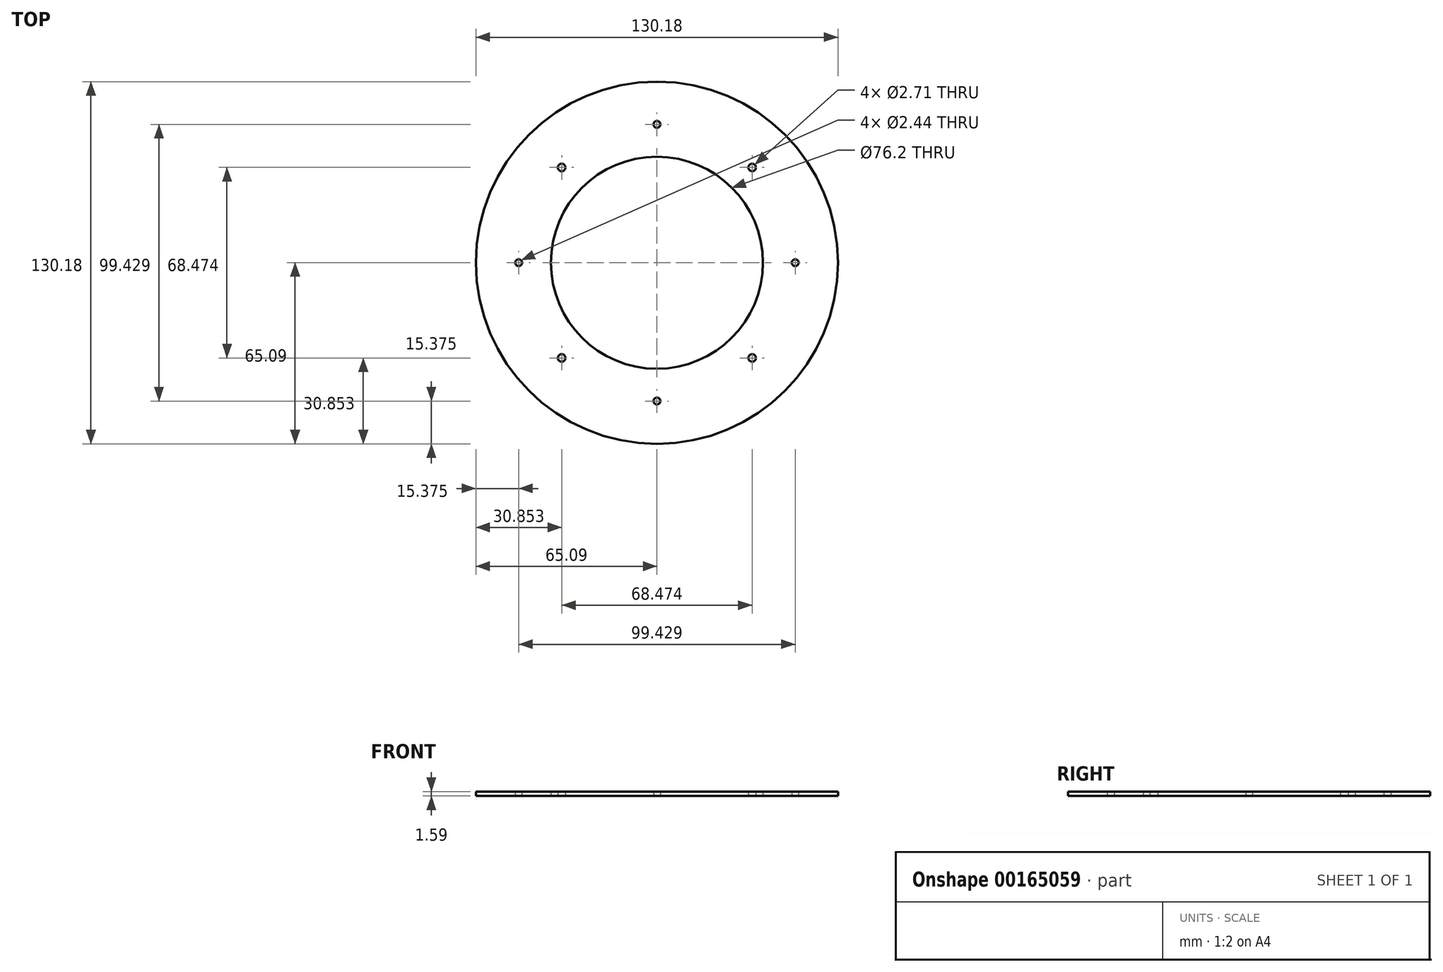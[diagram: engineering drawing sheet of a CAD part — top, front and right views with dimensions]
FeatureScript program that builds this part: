
annotation { "Feature Type Name" : "Feature", "Feature Type Description" : "" }
export const myFeature = defineFeature(function(context is Context, id is Id, definition is map)
    precondition{}
    {
        {
            var Q0;
            Q0=qCreatedBy(makeId("Top.planeOp"),FACE);
            var sketch = newSketch(context, id + "F0", { "sketchPlane" : qUnion([Q0])});
            skLineSegment(sketch, "E0.bottom", {"start": v(49.71, 0) * mm, "end": v(0, 49.71) * mm, "construction": true});
            skLineSegment(sketch, "E0.top", {"start": v(0, -49.71) * mm, "end": v(-49.71, 0) * mm, "construction": true});
            skLineSegment(sketch, "E0.left", {"start": v(49.71, 0) * mm, "end": v(0, -49.71) * mm, "construction": true});
            skLineSegment(sketch, "E0.right", {"start": v(0, 49.71) * mm, "end": v(-49.71, 0) * mm, "construction": true});
            skPoint(sketch, "E0.middle", {"position": v(0, 0) * mm});
            skCircle(sketch, "E1", {"center": v(0, 0) * mm, "radius": 38.1 * mm});
            skCircle(sketch, "E2", {"center": v(49.71, 0) * mm, "radius": 1.22 * mm});
            skCircle(sketch, "E3", {"center": v(0, 49.71) * mm, "radius": 1.22 * mm});
            skCircle(sketch, "E4", {"center": v(-49.71, 0) * mm, "radius": 1.22 * mm});
            skCircle(sketch, "E5", {"center": v(0, -49.71) * mm, "radius": 1.22 * mm});
            skCircle(sketch, "E6", {"center": v(0, 0) * mm, "radius": 65.09 * mm});
            skCircle(sketch, "E7", {"center": v(49.71, 0) * mm, "radius": 4.53 * mm, "construction": true});
            skLineSegment(sketch, "E8.bottom", {"start": v(-34.24, 34.24) * mm, "end": v(-34.24, -34.24) * mm, "construction": true});
            skLineSegment(sketch, "E8.top", {"start": v(34.24, 34.24) * mm, "end": v(34.24, -34.24) * mm, "construction": true});
            skLineSegment(sketch, "E8.left", {"start": v(-34.24, 34.24) * mm, "end": v(34.24, 34.24) * mm, "construction": true});
            skLineSegment(sketch, "E8.right", {"start": v(-34.24, -34.24) * mm, "end": v(34.24, -34.24) * mm, "construction": true});
            skCircle(sketch, "E9", {"center": v(-34.24, 34.24) * mm, "radius": 3.97 * mm, "construction": true});
            skCircle(sketch, "E10", {"center": v(-34.24, -34.24) * mm, "radius": 1.35 * mm});
            skCircle(sketch, "E11", {"center": v(-34.24, 34.24) * mm, "radius": 1.35 * mm});
            skCircle(sketch, "E12", {"center": v(34.24, 34.24) * mm, "radius": 1.35 * mm});
            skCircle(sketch, "E13", {"center": v(34.24, -34.24) * mm, "radius": 1.35 * mm});
            skCircle(sketch, "E14", {"center": v(0, 0) * mm, "radius": 52.39 * mm, "construction": true});
            skLineSegment(sketch, "E15", {"start": v(0, -49.71) * mm, "end": v(0, 0) * mm, "construction": true});
            skSolve(sketch);
        }
        {
            var Q0;
            Q0=makeQuery(id+"F0.imprint","IMPRINT",FACE,{"disambiguationData":[TD([[makeQuery(id+"F0.imprint","IMPRINT",EDGE,{"derivedFrom":sQuery(id+"F0.wireOp",EDGE,"E1")}),-1.0]])]});
            extrude(context, id + "F1", {"entities" : qUnion([Q0]), "depth" : 1.59 * mm});
        }
    });
